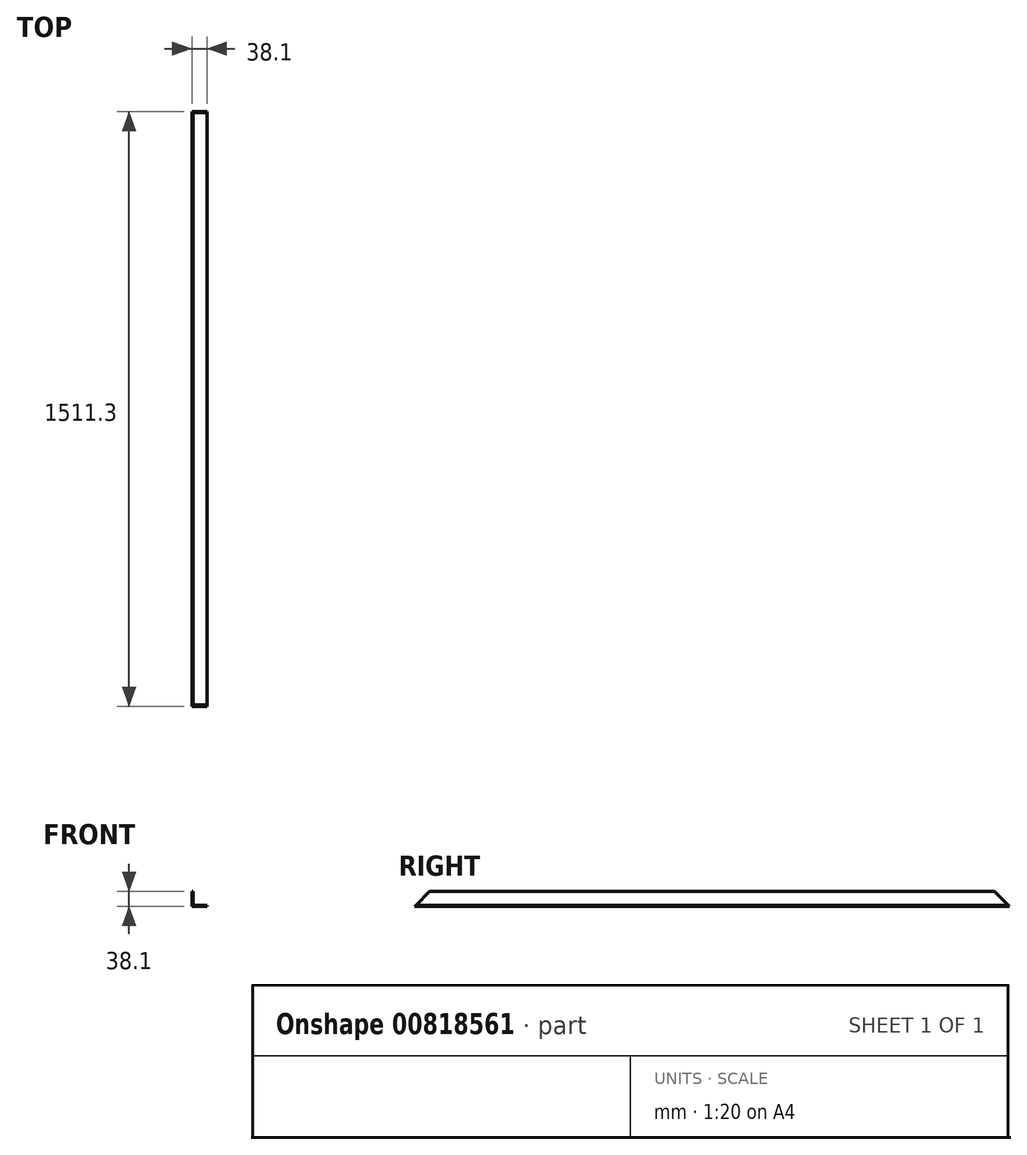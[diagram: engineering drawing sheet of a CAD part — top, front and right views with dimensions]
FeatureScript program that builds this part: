
annotation { "Feature Type Name" : "Feature", "Feature Type Description" : "" }
export const myFeature = defineFeature(function(context is Context, id is Id, definition is map)
    precondition{}
    {
        {
            var Q0;
            Q0=qCreatedBy(makeId("Front.planeOp"),FACE);
            var sketch = newSketch(context, id + "F0", { "sketchPlane" : qUnion([Q0])});
            skLineSegment(sketch, "E0", {"start": v(-21.73, 20.45) * mm, "end": v(-21.73, -17.65) * mm});
            skLineSegment(sketch, "E1", {"start": v(-21.73, -17.65) * mm, "end": v(16.37, -17.65) * mm});
            skLineSegment(sketch, "E2", {"start": v(16.37, -17.65) * mm, "end": v(16.37, -14.47) * mm});
            skLineSegment(sketch, "E3", {"start": v(16.37, -14.47) * mm, "end": v(-18.55, -14.47) * mm});
            skLineSegment(sketch, "E4", {"start": v(-18.55, -14.47) * mm, "end": v(-18.55, 20.45) * mm});
            skLineSegment(sketch, "E5", {"start": v(-18.55, 20.45) * mm, "end": v(-21.73, 20.45) * mm});
            skSolve(sketch);
        }
        {
            var Q0;
            Q0=makeQuery(id+"F0.imprint","IMPRINT",FACE,{"disambiguationData":[TD([[makeQuery(id+"F0.imprint","IMPRINT",EDGE,{"derivedFrom":sQuery(id+"F0.wireOp",EDGE,"E0")}),1.0]])]});
            extrude(context, id + "F1", {"entities" : qUnion([Q0]), "depth" : 1511.3 * mm, "offsetDistance" : 25.4 * mm});
        }
        {
            var Q0;
            Q0=makeQuery(id+"F1.opExtrude","SWEPT_FACE",FACE,{"disambiguationData":[OSD([sQuery(id+"F0.wireOp",EDGE,"E0")])]});
            var sketch = newSketch(context, id + "F2", { "sketchPlane" : qUnion([Q0])});
            skLineSegment(sketch, "E6", {"start": v(1511.3, -17.65) * mm, "end": v(1473.2, 20.45) * mm});
            skLineSegment(sketch, "E7", {"start": v(1473.2, 20.45) * mm, "end": v(1511.3, 20.45) * mm});
            skLineSegment(sketch, "E8", {"start": v(1511.3, 20.45) * mm, "end": v(1511.3, -17.65) * mm});
            skLineSegment(sketch, "E9", {"start": v(0, -17.65) * mm, "end": v(38.1, 20.45) * mm});
            skLineSegment(sketch, "E10", {"start": v(38.1, 20.45) * mm, "end": v(0, 20.45) * mm});
            skLineSegment(sketch, "E11", {"start": v(0, 20.45) * mm, "end": v(0, -17.65) * mm});
            skSolve(sketch);
        }
        {
            var Q0;
            Q0=qSketchRegion(id+"F2",true);
            extrude(context, id + "F3", {"entities" : qUnion([Q0]), "operationType" : NewBodyOperationType.REMOVE, "oppositeDirection" : true, "depth" : 38.1 * mm, "offsetDistance" : 25.4 * mm});
        }
    });
